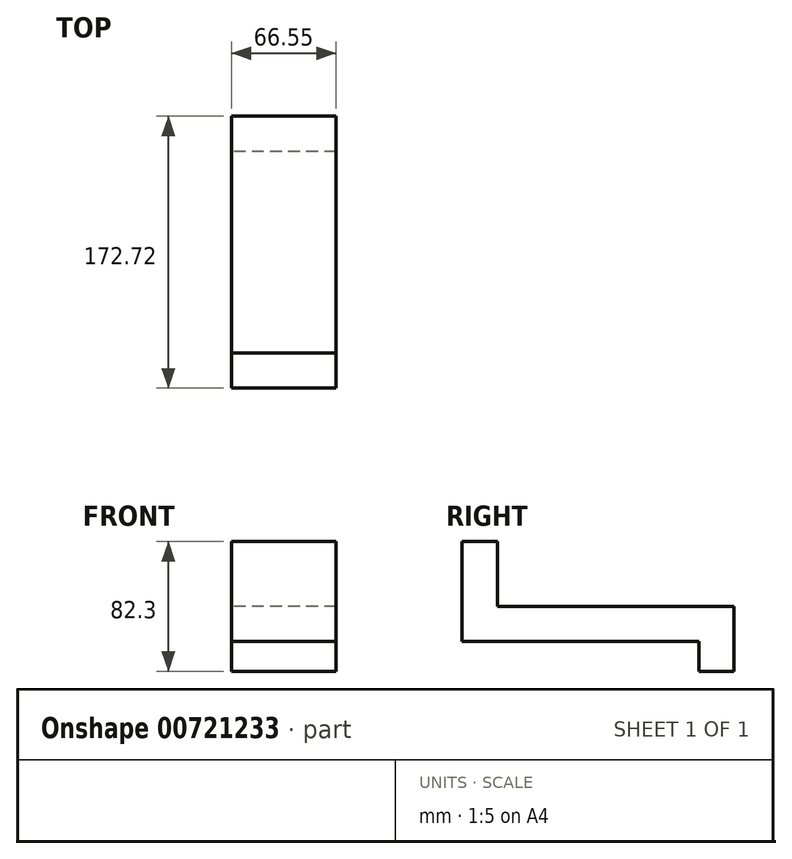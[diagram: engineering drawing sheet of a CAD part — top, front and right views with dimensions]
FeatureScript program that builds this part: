
annotation { "Feature Type Name" : "Feature", "Feature Type Description" : "" }
export const myFeature = defineFeature(function(context is Context, id is Id, definition is map)
    precondition{}
    {
        {
            var Q0;
            Q0=qCreatedBy(makeId("Right.planeOp"),FACE);
            var sketch = newSketch(context, id + "F0", { "sketchPlane" : qUnion([Q0])});
            skLineSegment(sketch, "E0", {"start": v(-67.1, 41.15) * mm, "end": v(-44.75, 41.15) * mm});
            skLineSegment(sketch, "E1", {"start": v(-44.75, 41.15) * mm, "end": v(-44.75, 0) * mm});
            skLineSegment(sketch, "E2", {"start": v(-44.75, 0) * mm, "end": v(105.62, 0) * mm});
            skLineSegment(sketch, "E3", {"start": v(105.62, 0) * mm, "end": v(105.62, -41.15) * mm});
            skLineSegment(sketch, "E4", {"start": v(105.62, -41.15) * mm, "end": v(83.27, -41.15) * mm});
            skLineSegment(sketch, "E5", {"start": v(83.27, -41.15) * mm, "end": v(83.27, -22.35) * mm});
            skLineSegment(sketch, "E6", {"start": v(83.27, -22.35) * mm, "end": v(-67.1, -22.35) * mm});
            skLineSegment(sketch, "E7", {"start": v(-67.1, -22.35) * mm, "end": v(-67.1, 41.15) * mm});
            skSolve(sketch);
        }
        {
            var Q0;
            Q0=makeQuery(id+"F0.imprint","IMPRINT",FACE,{"disambiguationData":[TD([[makeQuery(id+"F0.imprint","IMPRINT",EDGE,{"derivedFrom":sQuery(id+"F0.wireOp",EDGE,"E0")}),-1.0]])]});
            extrude(context, id + "F1", {"entities" : qUnion([Q0]), "depth" : 66.55 * mm, "offsetDistance" : 25.4 * mm});
        }
    });
